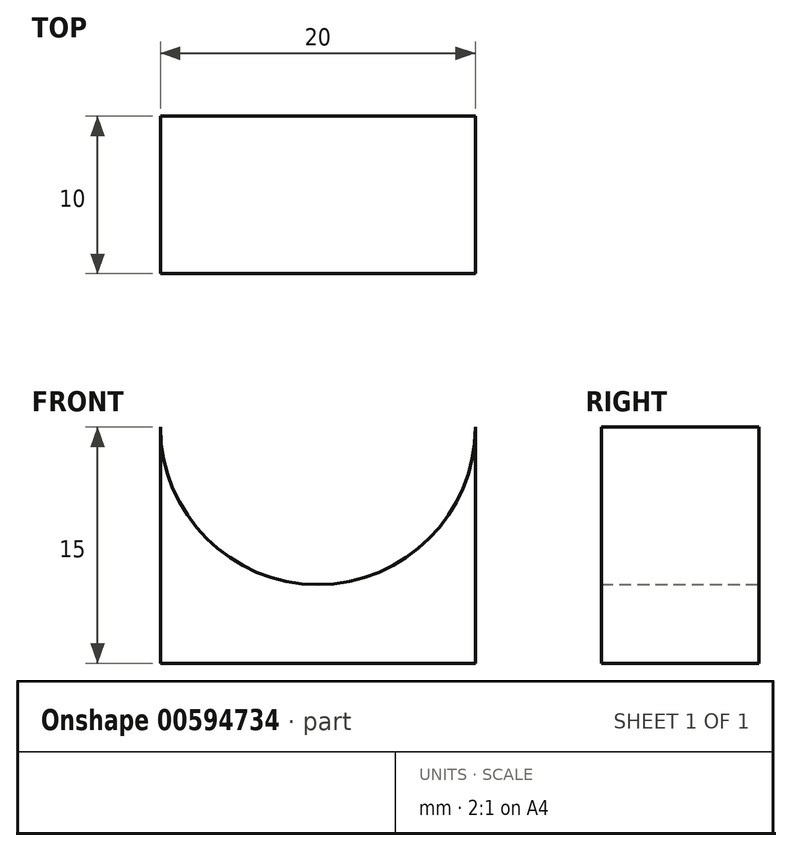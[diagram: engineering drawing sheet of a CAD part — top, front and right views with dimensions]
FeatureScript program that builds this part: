
annotation { "Feature Type Name" : "Feature", "Feature Type Description" : "" }
export const myFeature = defineFeature(function(context is Context, id is Id, definition is map)
    precondition{}
    {
        {
            var Q0;
            Q0=qCreatedBy(makeId("Front.planeOp"),FACE);
            var sketch = newSketch(context, id + "F0", { "sketchPlane" : qUnion([Q0])});
            skArc(sketch, "E0", {"start": v(-10, 0) * mm, "mid": v(0, -10) * mm, "end": v(10, 0) * mm});
            skLineSegment(sketch, "E1", {"start": v(-10, 0) * mm, "end": v(-10, -15) * mm});
            skLineSegment(sketch, "E2", {"start": v(10, 0) * mm, "end": v(10, -15) * mm});
            skLineSegment(sketch, "E3", {"start": v(-10, -15) * mm, "end": v(10, -15) * mm});
            skSolve(sketch);
        }
        {
            var Q0;
            Q0=qSketchRegion(id+"F0",true);
            extrude(context, id + "F1", {"entities" : qUnion([Q0]), "depth" : 10 * mm, "offsetDistance" : 25 * mm});
        }
    });
